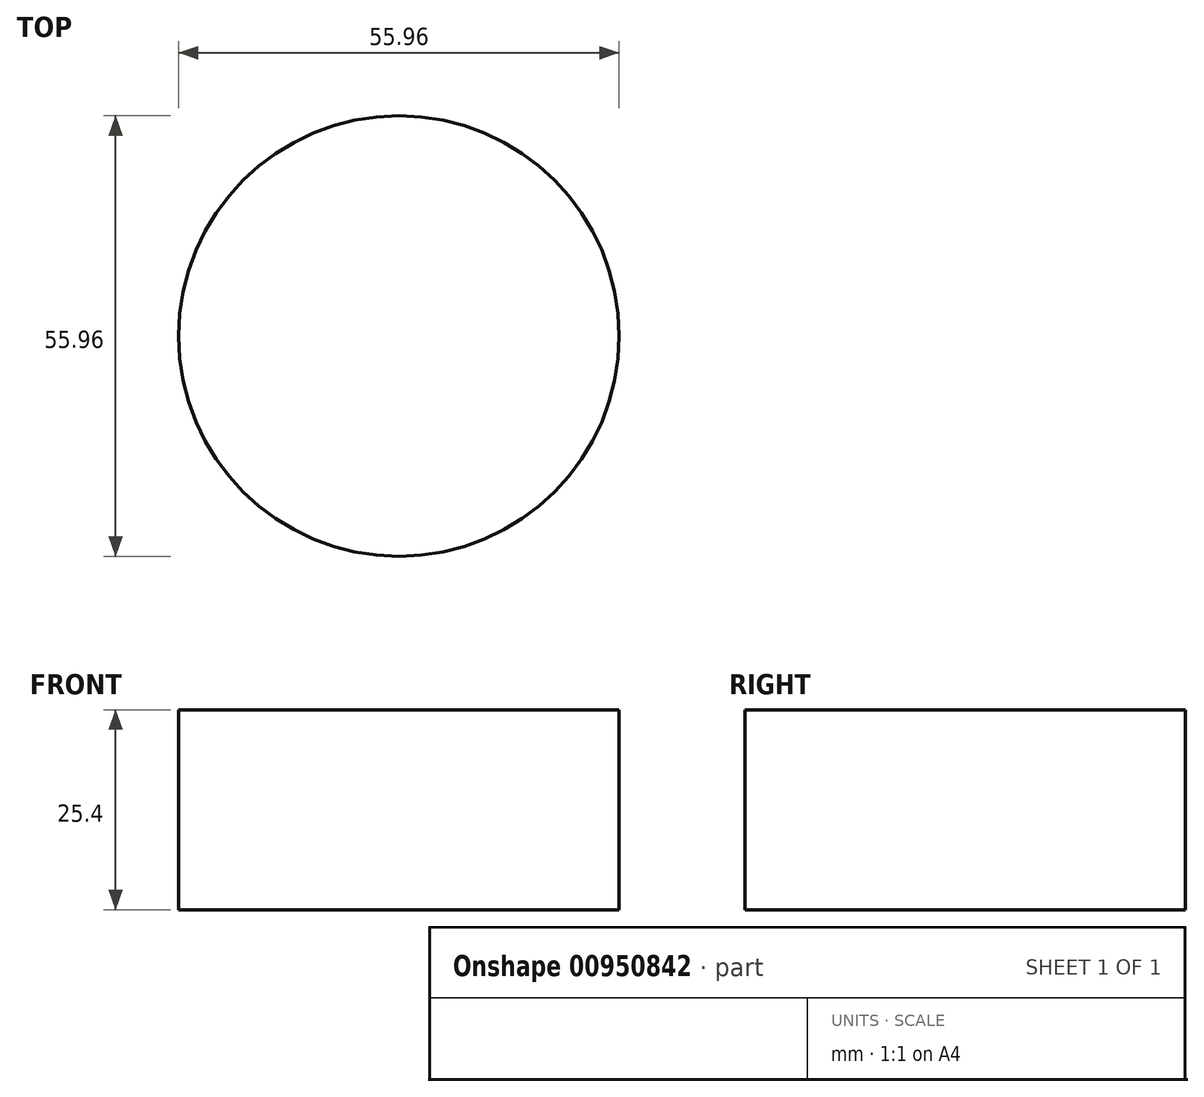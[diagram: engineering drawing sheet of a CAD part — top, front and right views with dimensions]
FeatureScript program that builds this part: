
annotation { "Feature Type Name" : "Feature", "Feature Type Description" : "" }
export const myFeature = defineFeature(function(context is Context, id is Id, definition is map)
    precondition{}
    {
        {
            var Q0;
            Q0=qCreatedBy(makeId("Top.planeOp"),FACE);
            var sketch = newSketch(context, id + "F0", { "sketchPlane" : qUnion([Q0])});
            skCircle(sketch, "E0", {"center": v(0, 1.55) * mm, "radius": 27.98 * mm});
            skSolve(sketch);
        }
        {
            var Q0;
            Q0 = qSketchRegion(id + "F0", true);
            extrude(context, id + "F1", {"entities" : qUnion([Q0]), "depth" : 25.4 * mm, "offsetDistance" : 25.4 * mm});
        }
    });
